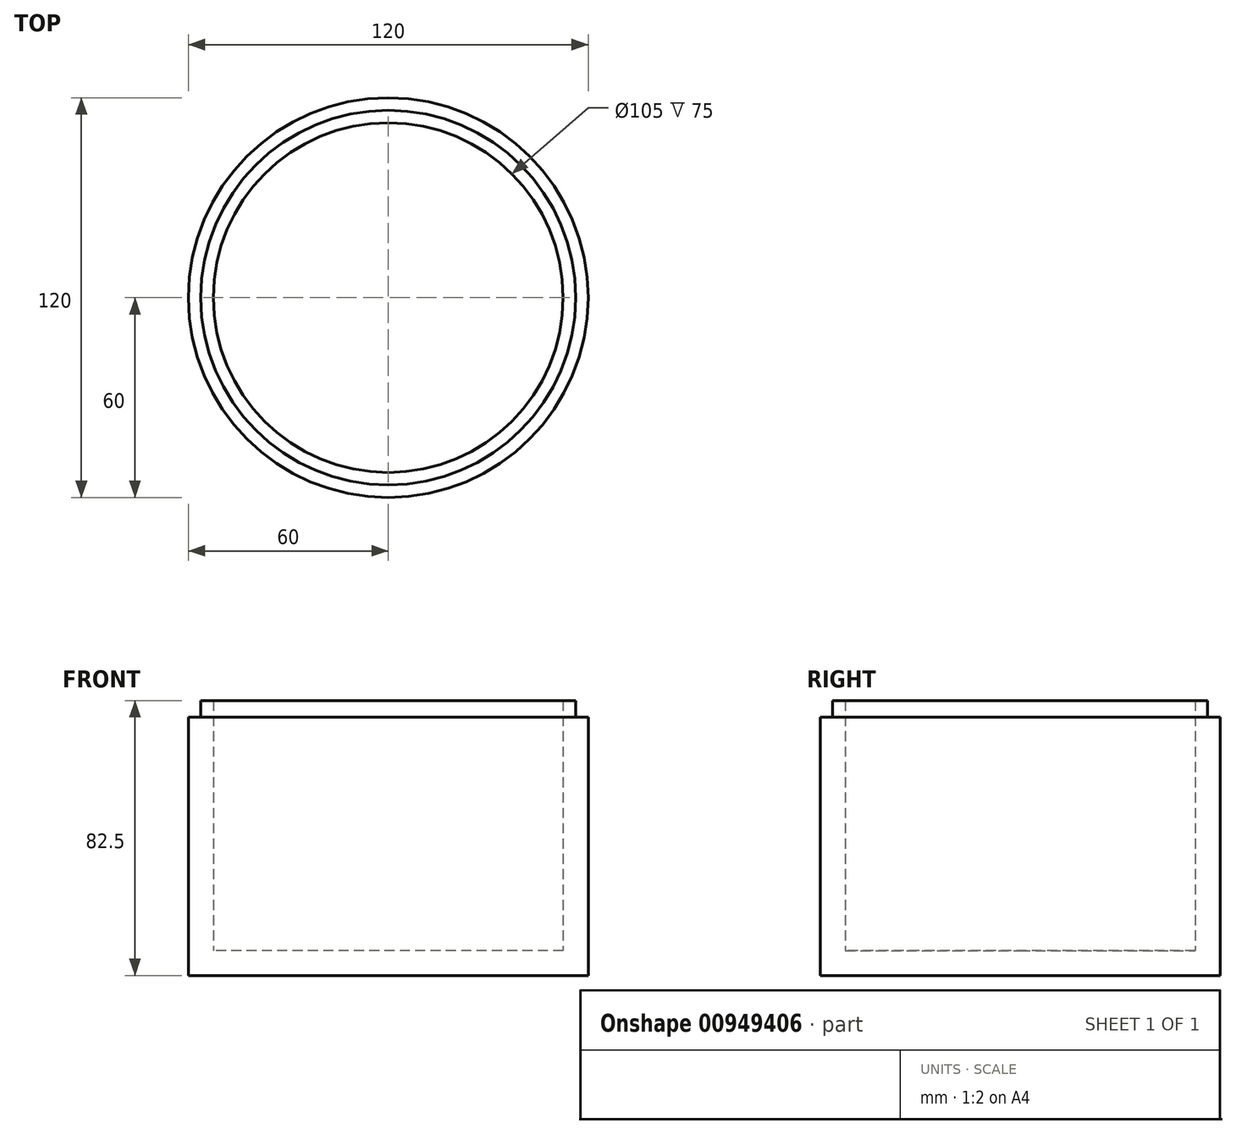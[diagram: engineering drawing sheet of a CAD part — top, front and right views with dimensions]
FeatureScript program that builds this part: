
annotation { "Feature Type Name" : "Feature", "Feature Type Description" : "" }
export const myFeature = defineFeature(function(context is Context, id is Id, definition is map)
    precondition{}
    {
        {
            var Q0;
            Q0=qCreatedBy(makeId("Top.planeOp"),FACE);
            var sketch = newSketch(context, id + "F0", { "sketchPlane" : qUnion([Q0])});
            skCircle(sketch, "E0", {"center": v(0, 0) * mm, "radius": 60 * mm});
            skSolve(sketch);
        }
        {
            var Q0;
            Q0 = qSketchRegion(id + "F0", true);
            extrude(context, id + "F1", {"entities" : qUnion([Q0]), "depth" : 7.5 * mm, "offsetDistance" : 25 * mm});
        }
        {
            var Q0;
            Q0=makeQuery(id+"F1.opExtrude","CAP_FACE",FACE,{"disambiguationData":[OSD([sQuery(id+"F0.wireOp",EDGE,"E0")])],"isStart":false});
            var sketch = newSketch(context, id + "F2", { "sketchPlane" : qUnion([Q0])});
            skCircle(sketch, "E1", {"center": v(0, 0) * mm, "radius": 52.5 * mm});
            skSolve(sketch);
        }
        {
            var Q0;
            Q0=makeQuery(id+"F2.imprint","IMPRINT",FACE,{"disambiguationData":[TD([[makeQuery(id+"F2.imprint","IMPRINT",EDGE,{"derivedFrom":sQuery(id+"F2.wireOp",EDGE,"E1")}),-1.0]])]});
            extrude(context, id + "F3", {"entities" : qUnion([Q0]), "operationType" : NewBodyOperationType.ADD, "depth" : 75 * mm, "offsetDistance" : 25 * mm});
        }
        {
            var Q0;
            Q0=makeQuery(id+"F3.opExtrude","CAP_FACE",FACE,{"disambiguationData":[OSD([sQuery(id+"F0.wireOp",EDGE,"E0"),sQuery(id+"F2.wireOp",EDGE,"E1")])],"isStart":false});
            var sketch = newSketch(context, id + "F4", { "sketchPlane" : qUnion([Q0])});
            skCircle(sketch, "E2", {"center": v(0, 0) * mm, "radius": 56.25 * mm});
            skSolve(sketch);
        }
        {
            var Q0;
            Q0=makeQuery(id+"F4.imprint","IMPRINT",FACE,{"disambiguationData":[TD([[makeQuery(id+"F4.imprint","IMPRINT",EDGE,{"derivedFrom":sQuery(id+"F4.wireOp",EDGE,"E2")}),-1.0]])]});
            extrude(context, id + "F5", {"entities" : qUnion([Q0]), "operationType" : NewBodyOperationType.REMOVE, "oppositeDirection" : true, "depth" : 5 * mm, "offsetDistance" : 25 * mm});
        }
    });
